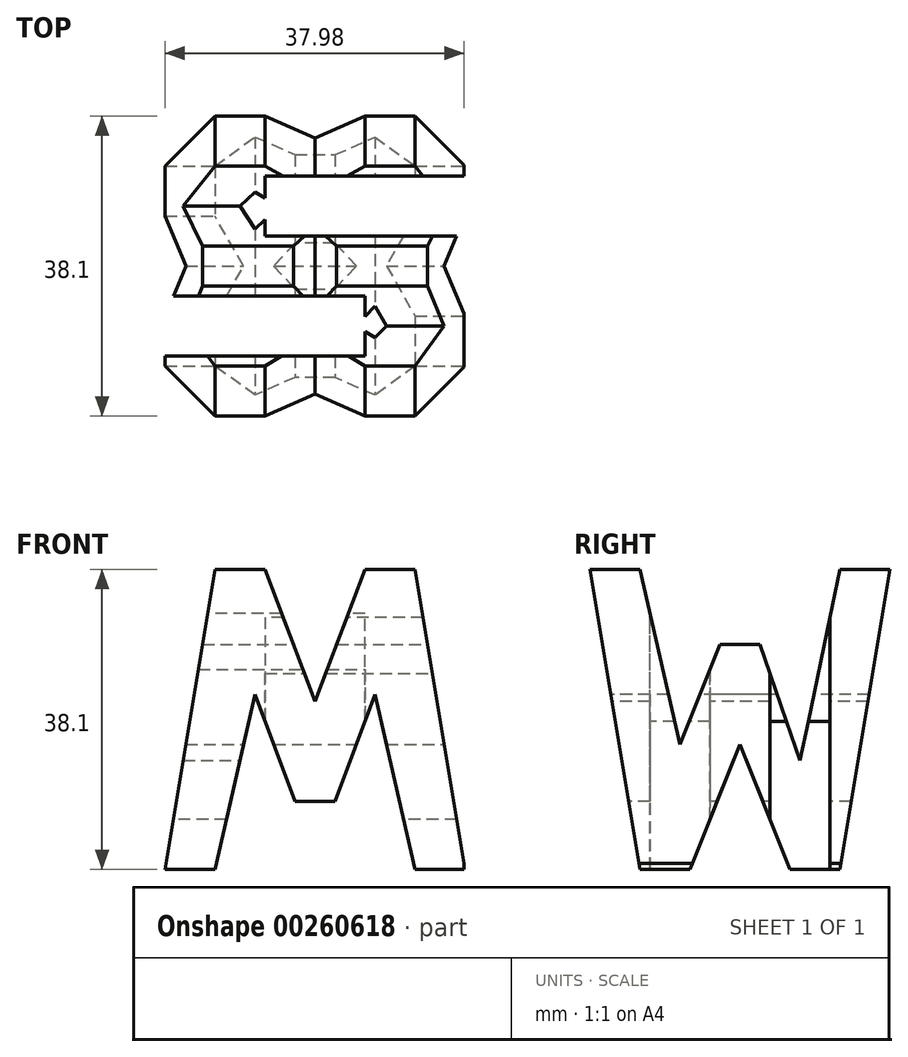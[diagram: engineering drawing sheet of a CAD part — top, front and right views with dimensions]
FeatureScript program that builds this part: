
annotation { "Feature Type Name" : "Feature", "Feature Type Description" : "" }
export const myFeature = defineFeature(function(context is Context, id is Id, definition is map)
    precondition{}
    {
        {
            var Q0;
            Q0=qCreatedBy(makeId("Front.planeOp"),FACE);
            var sketch = newSketch(context, id + "F0", { "sketchPlane" : qUnion([Q0])});
            skLineSegment(sketch, "E0", {"start": v(0, 38.1) * mm, "end": v(0, 0) * mm});
            skLineSegment(sketch, "E1", {"start": v(0, 0) * mm, "end": v(37.98, 0) * mm});
            skLineSegment(sketch, "E2", {"start": v(37.98, 0) * mm, "end": v(37.98, 38.1) * mm});
            skLineSegment(sketch, "E3", {"start": v(37.98, 38.1) * mm, "end": v(0, 38.1) * mm});
            skSolve(sketch);
        }
        {
            var Q0;
            Q0 = qSketchRegion(id + "F0", true);
            extrude(context, id + "F1", {"entities" : qUnion([Q0]), "depth" : 38.1 * mm});
        }
        {
            var Q0;
            Q0=qCreatedBy(makeId("Front.planeOp"),FACE);
            cPlane(context, id + "F2", {"entities" : qUnion([Q0]), "cplaneType" : CPlaneType.OFFSET, "offset" : 38.1 * mm, "width" : 152.4 * mm, "height" : 152.4 * mm});
        }
        {
            var Q0;
            Q0=qCreatedBy(makeId("Right.planeOp"),FACE);
            cPlane(context, id + "F3", {"entities" : qUnion([Q0]), "cplaneType" : CPlaneType.OFFSET, "offset" : 38.1 * mm, "width" : 152.4 * mm, "height" : 152.4 * mm});
        }
        {
            var Q0;
            Q0=qCreatedBy(makeId("Top.planeOp"),FACE);
            cPlane(context, id + "F4", {"entities" : qUnion([Q0]), "cplaneType" : CPlaneType.OFFSET, "offset" : 38.1 * mm, "width" : 152.4 * mm, "height" : 152.4 * mm});
        }
        {
            var Q0;
            Q0=qCreatedBy(id+"F3.planeOp",FACE);
            var sketch = newSketch(context, id + "F5", { "sketchPlane" : qUnion([Q0])});
            skLineSegment(sketch, "E4", {"start": v(0, 38.1) * mm, "end": v(-38.1, 38.1) * mm});
            skLineSegment(sketch, "E5", {"start": v(-38.1, 38.1) * mm, "end": v(-38.1, 0) * mm});
            skLineSegment(sketch, "E6", {"start": v(-38.1, 0) * mm, "end": v(0, 0) * mm});
            skLineSegment(sketch, "E7", {"start": v(0, 0) * mm, "end": v(0, 38.1) * mm});
            skLineSegment(sketch, "E8", {"start": v(-38.1, 38.1) * mm, "end": v(-31.75, 0) * mm});
            skLineSegment(sketch, "E9", {"start": v(-31.75, 0) * mm, "end": v(-25.4, 0) * mm});
            skLineSegment(sketch, "E10", {"start": v(-25.4, 0) * mm, "end": v(-19.05, 15.87) * mm});
            skLineSegment(sketch, "E11", {"start": v(-19.05, 0) * mm, "end": v(-6.35, 0) * mm});
            skLineSegment(sketch, "E12", {"start": v(-6.35, 0) * mm, "end": v(0, 38.1) * mm});
            skLineSegment(sketch, "E13", {"start": v(-6.35, 38.1) * mm, "end": v(-11.43, 13.83) * mm});
            skLineSegment(sketch, "E14", {"start": v(-11.43, 13.83) * mm, "end": v(-16.51, 28.57) * mm});
            skLineSegment(sketch, "E15", {"start": v(-16.51, 28.57) * mm, "end": v(-21.59, 28.57) * mm});
            skLineSegment(sketch, "E16", {"start": v(-21.6, 28.57) * mm, "end": v(-26.67, 15.87) * mm});
            skLineSegment(sketch, "E17", {"start": v(-26.67, 15.87) * mm, "end": v(-31.75, 38.1) * mm});
            skLineSegment(sketch, "E18", {"start": v(-19.05, 15.87) * mm, "end": v(-12.7, 0) * mm});
            skLineSegment(sketch, "E19", {"start": v(-12.7, 0) * mm, "end": v(-6.35, 0) * mm});
            skSolve(sketch);
        }
        {
            var Q0;
            {var subQ0=sQuery(id+"F5.wireOp",EDGE,"E5");Q0=makeQuery(id+"F5.imprint","IMPRINT",FACE,{"disambiguationData":[TD([[makeQuery(id+"F5.imprint","IMPRINT",EDGE,{"derivedFrom":subQ0}),1.0]])]});}
            var Q1;
            {var subQ0=sQuery(id+"F5.wireOp",EDGE,"E13");Q1=makeQuery(id+"F5.imprint","IMPRINT",FACE,{"disambiguationData":[TD([[makeQuery(id+"F5.imprint","IMPRINT",EDGE,{"derivedFrom":subQ0}),-1.0]])]});}
            var Q2;
            {var subQ0=sQuery(id+"F5.wireOp",EDGE,"E10");Q2=makeQuery(id+"F5.imprint","IMPRINT",FACE,{"disambiguationData":[TD([[makeQuery(id+"F5.imprint","IMPRINT",EDGE,{"derivedFrom":subQ0}),-1.0]])]});}
            var Q3;
            {var subQ0=sQuery(id+"F5.wireOp",EDGE,"E7");Q3=makeQuery(id+"F5.imprint","IMPRINT",FACE,{"disambiguationData":[TD([[makeQuery(id+"F5.imprint","IMPRINT",EDGE,{"derivedFrom":subQ0}),1.0]])]});}
            extrude(context, id + "F6", {"entities" : qUnion([Q0, Q1, Q2, Q3]), "operationType" : NewBodyOperationType.REMOVE, "oppositeDirection" : true, "depth" : 38.1 * mm});
        }
        {
            var Q0;
            Q0=qCreatedBy(id+"F2.planeOp",FACE);
            var sketch = newSketch(context, id + "F7", { "sketchPlane" : qUnion([Q0])});
            skLineSegment(sketch, "E20.bottom", {"start": v(0, 0) * mm, "end": v(38.1, 0) * mm});
            skLineSegment(sketch, "E20.top", {"start": v(0, 38.1) * mm, "end": v(38.1, 38.1) * mm});
            skLineSegment(sketch, "E20.left", {"start": v(0, 0) * mm, "end": v(0, 38.1) * mm});
            skLineSegment(sketch, "E20.right", {"start": v(38.1, 0) * mm, "end": v(38.1, 38.1) * mm});
            skLineSegment(sketch, "E21", {"start": v(0, 0) * mm, "end": v(6.35, 38.1) * mm});
            skLineSegment(sketch, "E22", {"start": v(6.35, 38.1) * mm, "end": v(12.7, 38.1) * mm});
            skLineSegment(sketch, "E23", {"start": v(12.7, 38.1) * mm, "end": v(19.05, 21.32) * mm});
            skLineSegment(sketch, "E24", {"start": v(19.05, 21.32) * mm, "end": v(25.4, 38.1) * mm});
            skLineSegment(sketch, "E25", {"start": v(25.4, 38.1) * mm, "end": v(31.75, 38.1) * mm});
            skLineSegment(sketch, "E26", {"start": v(31.75, 38.1) * mm, "end": v(38.1, 0) * mm});
            skLineSegment(sketch, "E27", {"start": v(31.75, 0) * mm, "end": v(26.67, 22.23) * mm});
            skLineSegment(sketch, "E28", {"start": v(26.67, 22.23) * mm, "end": v(21.6, 8.62) * mm});
            skLineSegment(sketch, "E29", {"start": v(21.6, 8.62) * mm, "end": v(16.51, 8.62) * mm});
            skLineSegment(sketch, "E30", {"start": v(16.51, 8.62) * mm, "end": v(11.43, 22.23) * mm});
            skLineSegment(sketch, "E31", {"start": v(11.43, 22.23) * mm, "end": v(6.35, 0) * mm});
            skSolve(sketch);
        }
        {
            var Q0;
            {var subQ0=sQuery(id+"F7.wireOp",EDGE,"E27");Q0=makeQuery(id+"F7.imprint","IMPRINT",FACE,{"disambiguationData":[TD([[makeQuery(id+"F7.imprint","IMPRINT",EDGE,{"derivedFrom":subQ0}),1.0]])]});}
            var Q1;
            {var subQ0=sQuery(id+"F7.wireOp",EDGE,"E23");Q1=makeQuery(id+"F7.imprint","IMPRINT",FACE,{"disambiguationData":[TD([[makeQuery(id+"F7.imprint","IMPRINT",EDGE,{"derivedFrom":subQ0}),1.0]])]});}
            var Q2;
            {var subQ0=sQuery(id+"F7.wireOp",EDGE,"E20.left");Q2=makeQuery(id+"F7.imprint","IMPRINT",FACE,{"disambiguationData":[TD([[makeQuery(id+"F7.imprint","IMPRINT",EDGE,{"derivedFrom":subQ0}),-1.0]])]});}
            var Q3;
            {var subQ0=sQuery(id+"F7.wireOp",EDGE,"E20.right");Q3=makeQuery(id+"F7.imprint","IMPRINT",FACE,{"disambiguationData":[TD([[makeQuery(id+"F7.imprint","IMPRINT",EDGE,{"derivedFrom":subQ0}),1.0]])]});}
            extrude(context, id + "F8", {"entities" : qUnion([Q0, Q1, Q2, Q3]), "operationType" : NewBodyOperationType.REMOVE, "oppositeDirection" : true, "depth" : 38.1 * mm});
        }
        {
            var Q0;
            Q0=qCreatedBy(id+"F4.planeOp",FACE);
            var sketch = newSketch(context, id + "F9", { "sketchPlane" : qUnion([Q0])});
            skLineSegment(sketch, "E32.bottom", {"start": v(0, -38.1) * mm, "end": v(38.1, -38.1) * mm});
            skLineSegment(sketch, "E32.top", {"start": v(0, 0) * mm, "end": v(38.1, 0) * mm});
            skLineSegment(sketch, "E32.left", {"start": v(0, -38.1) * mm, "end": v(0, 0) * mm});
            skLineSegment(sketch, "E32.right", {"start": v(38.1, -38.1) * mm, "end": v(38.1, 0) * mm});
            skLineSegment(sketch, "E33", {"start": v(38.1, -7.62) * mm, "end": v(12.7, -7.62) * mm});
            skLineSegment(sketch, "E34", {"start": v(12.7, -7.62) * mm, "end": v(12.7, -15.24) * mm});
            skLineSegment(sketch, "E35", {"start": v(12.7, -15.24) * mm, "end": v(38.1, -15.24) * mm});
            skLineSegment(sketch, "E36", {"start": v(0, -22.86) * mm, "end": v(25.4, -22.86) * mm});
            skLineSegment(sketch, "E37", {"start": v(25.4, -22.86) * mm, "end": v(25.4, -30.48) * mm});
            skLineSegment(sketch, "E38", {"start": v(25.4, -30.48) * mm, "end": v(0, -30.48) * mm});
            skSolve(sketch);
        }
        {
            var Q0;
            {var subQ0=sQuery(id+"F9.wireOp",EDGE,"E33");Q0=makeQuery(id+"F9.imprint","IMPRINT",FACE,{"disambiguationData":[TD([[makeQuery(id+"F9.imprint","IMPRINT",EDGE,{"derivedFrom":subQ0}),1.0]])]});}
            var Q1;
            {var subQ0=sQuery(id+"F9.wireOp",EDGE,"E36");Q1=makeQuery(id+"F9.imprint","IMPRINT",FACE,{"disambiguationData":[TD([[makeQuery(id+"F9.imprint","IMPRINT",EDGE,{"derivedFrom":subQ0}),-1.0]])]});}
            extrude(context, id + "F10", {"entities" : qUnion([Q0, Q1]), "operationType" : NewBodyOperationType.REMOVE, "oppositeDirection" : true, "depth" : 38.1 * mm});
        }
    });
